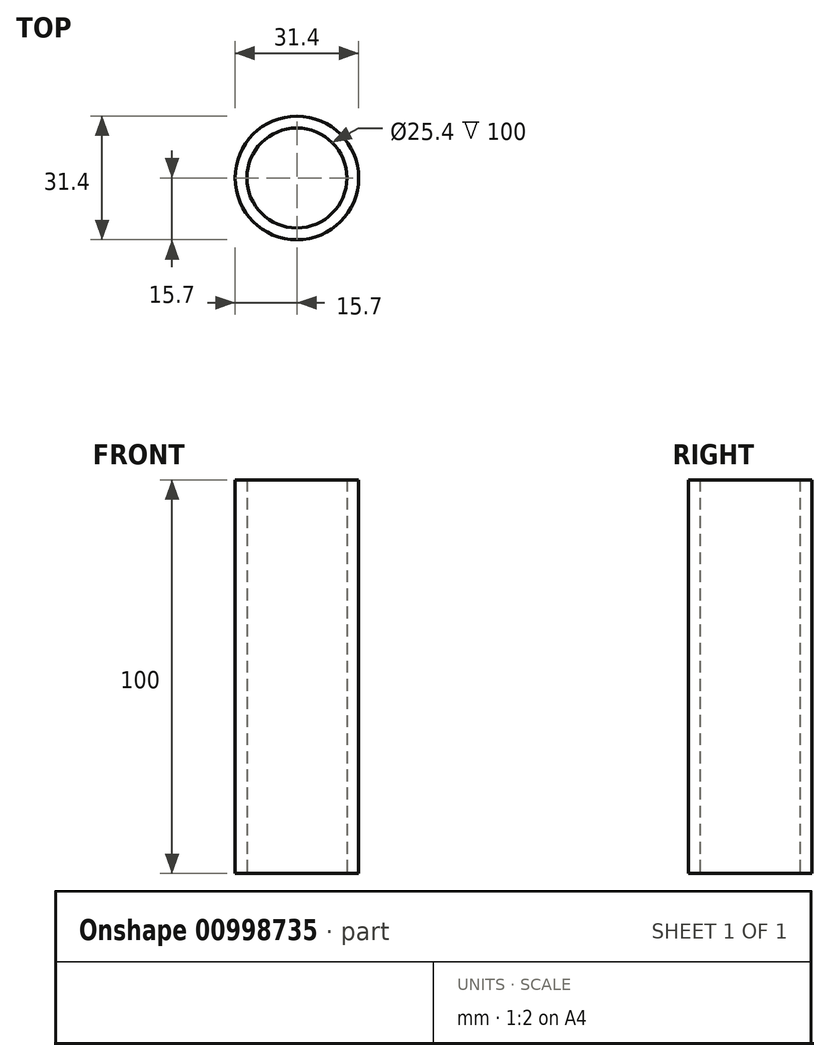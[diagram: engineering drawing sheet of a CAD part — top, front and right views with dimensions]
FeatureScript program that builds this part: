
annotation { "Feature Type Name" : "Feature", "Feature Type Description" : "" }
export const myFeature = defineFeature(function(context is Context, id is Id, definition is map)
    precondition{}
    {
        {
            var Q0;
            Q0=qCreatedBy(makeId("Top.planeOp"),FACE);
            var sketch = newSketch(context, id + "F0", { "sketchPlane" : qUnion([Q0])});
            skCircle(sketch, "E0", {"center": v(0, 0) * mm, "radius": 15.7 * mm});
            skCircle(sketch, "E1", {"center": v(0, 0) * mm, "radius": 12.7 * mm});
            skSolve(sketch);
        }
        {
            var Q0;
            Q0 = qSketchRegion(id + "F0", true);
            extrude(context, id + "F1", {"entities" : qUnion([Q0]), "depth" : 100 * mm, "offsetDistance" : 25 * mm});
        }
    });
